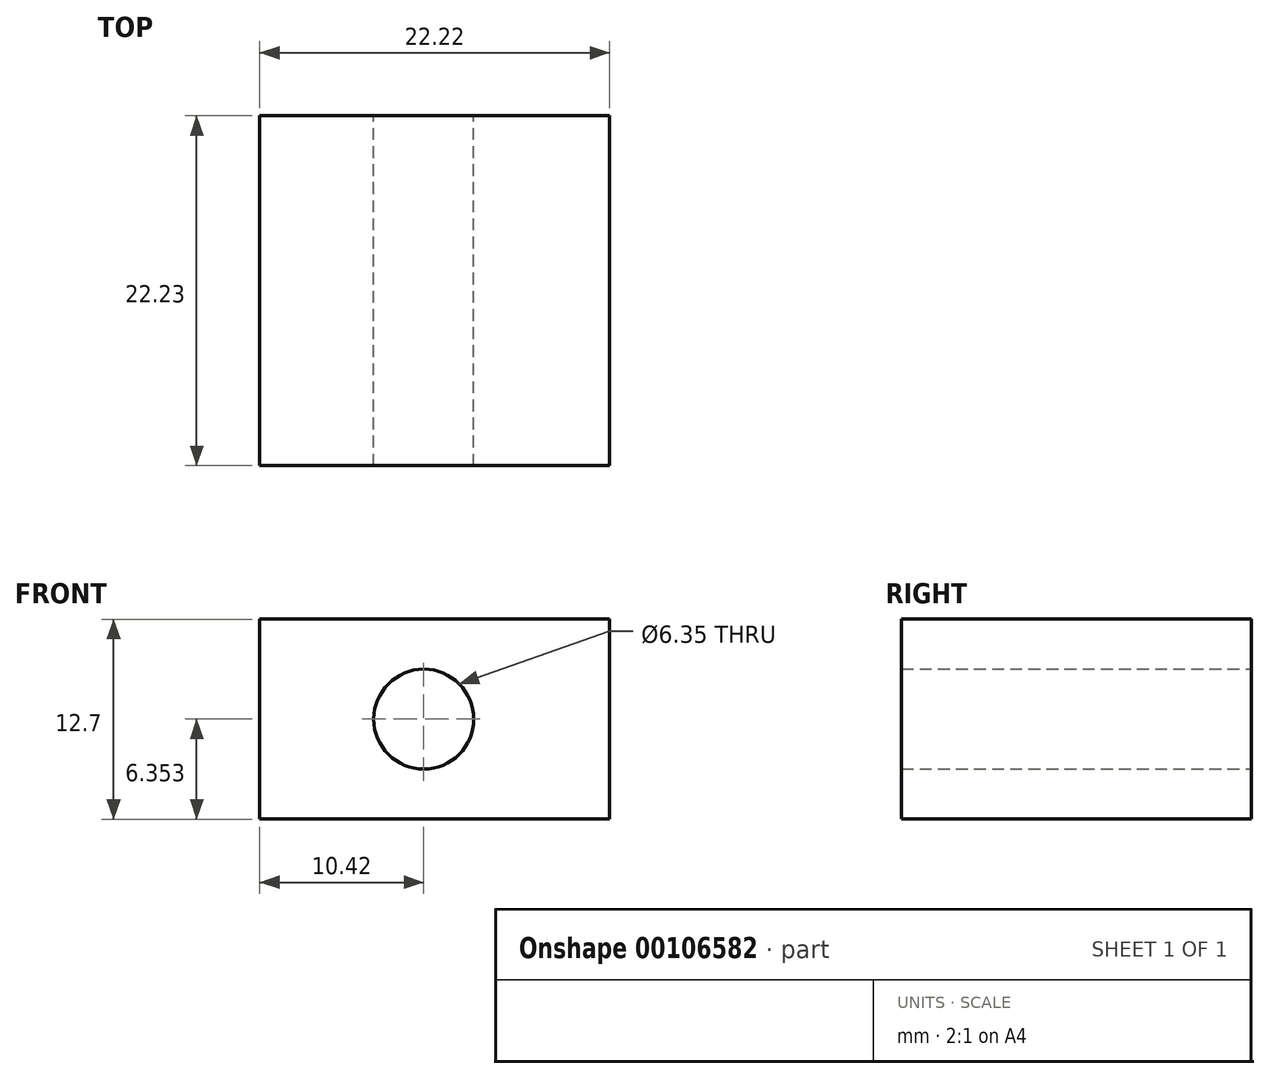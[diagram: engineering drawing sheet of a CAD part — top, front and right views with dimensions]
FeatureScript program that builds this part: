
annotation { "Feature Type Name" : "Feature", "Feature Type Description" : "" }
export const myFeature = defineFeature(function(context is Context, id is Id, definition is map)
    precondition{}
    {
        {
            var Q0;
            Q0=qCreatedBy(makeId("Front.planeOp"),FACE);
            var sketch = newSketch(context, id + "F0", { "sketchPlane" : qUnion([Q0])});
            skLineSegment(sketch, "E0.bottom", {"start": v(-62.84, 11.7) * mm, "end": v(-40.62, 11.7) * mm});
            skLineSegment(sketch, "E0.top", {"start": v(-62.84, -1) * mm, "end": v(-40.62, -1) * mm});
            skLineSegment(sketch, "E0.left", {"start": v(-62.84, 11.7) * mm, "end": v(-62.84, -1) * mm});
            skLineSegment(sketch, "E0.right", {"start": v(-40.62, 11.7) * mm, "end": v(-40.62, -1) * mm});
            skCircle(sketch, "E1", {"center": v(-52.42, 5.35) * mm, "radius": 3.18 * mm});
            skSolve(sketch);
        }
        {
            var Q0;
            Q0=makeQuery(id+"F0.imprint","IMPRINT",FACE,{"disambiguationData":[TD([[makeQuery(id+"F0.imprint","IMPRINT",EDGE,{"derivedFrom":sQuery(id+"F0.wireOp",EDGE,"E0.bottom")}),-1.0]])]});
            extrude(context, id + "F1", {"entities" : qUnion([Q0]), "depth" : 22.22 * mm});
        }
    });
